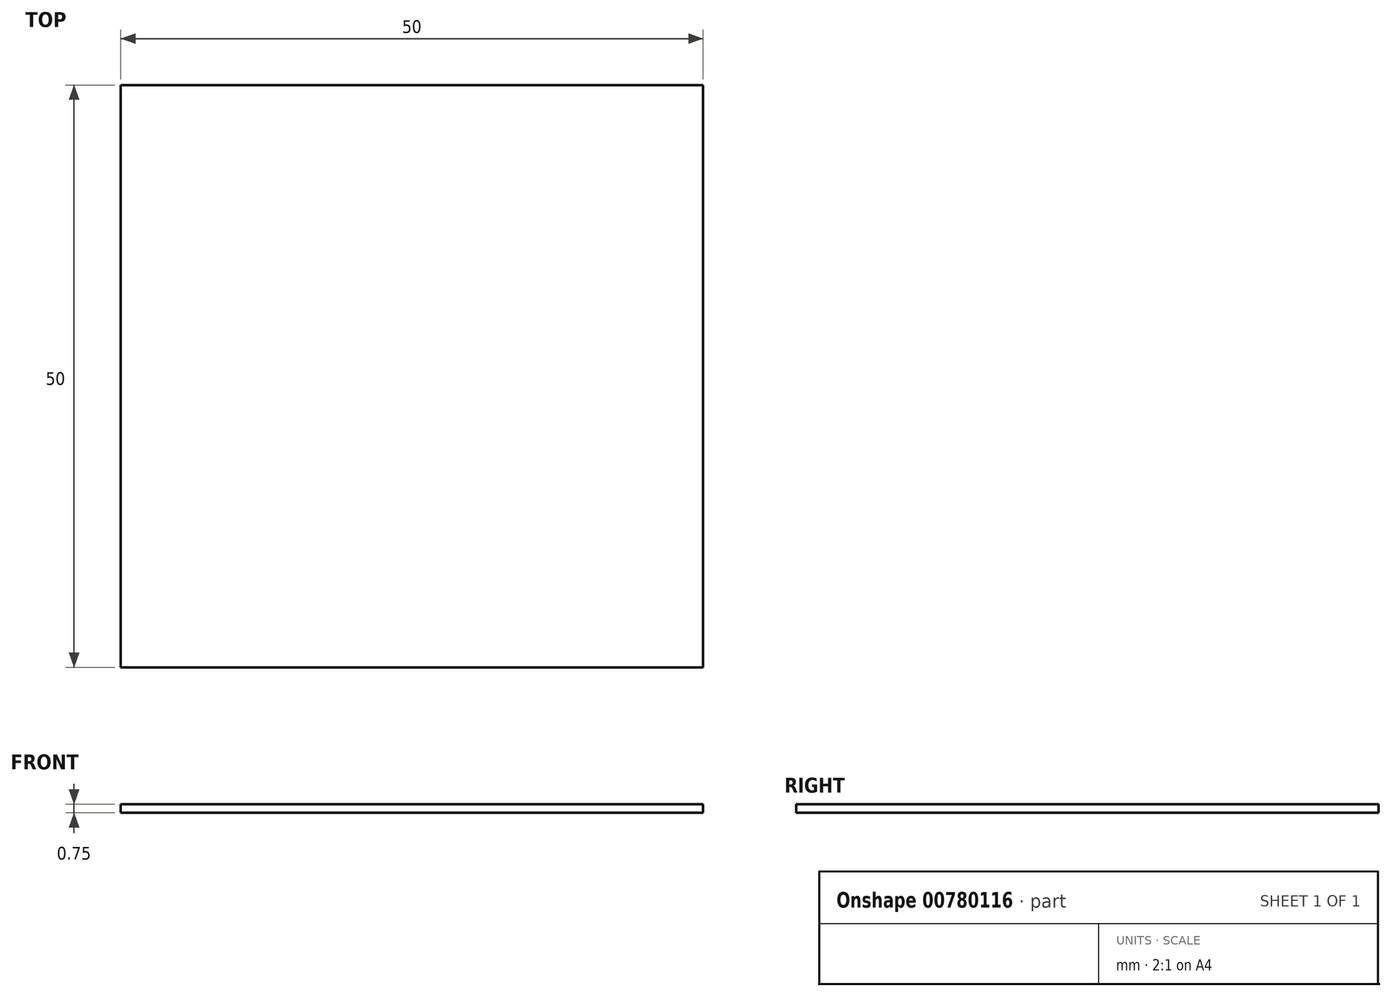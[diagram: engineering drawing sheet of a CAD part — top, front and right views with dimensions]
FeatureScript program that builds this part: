
annotation { "Feature Type Name" : "Feature", "Feature Type Description" : "" }
export const myFeature = defineFeature(function(context is Context, id is Id, definition is map)
    precondition{}
    {
        {
            var Q0;
            Q0=qCreatedBy(makeId("Top.planeOp"),FACE);
            var sketch = newSketch(context, id + "F0", { "sketchPlane" : qUnion([Q0])});
            skLineSegment(sketch, "E0.bottom", {"start": v(0, 0) * mm, "end": v(50, 0) * mm});
            skLineSegment(sketch, "E0.top", {"start": v(0, 50) * mm, "end": v(50, 50) * mm});
            skLineSegment(sketch, "E0.left", {"start": v(0, 0) * mm, "end": v(0, 50) * mm});
            skLineSegment(sketch, "E0.right", {"start": v(50, 0) * mm, "end": v(50, 50) * mm});
            skSolve(sketch);
        }
        {
            var Q0;
            Q0 = qSketchRegion(id + "F0", true);
            extrude(context, id + "F1", {"entities" : qUnion([Q0]), "depth" : 0.75 * mm, "offsetDistance" : 25 * mm});
        }
    });
